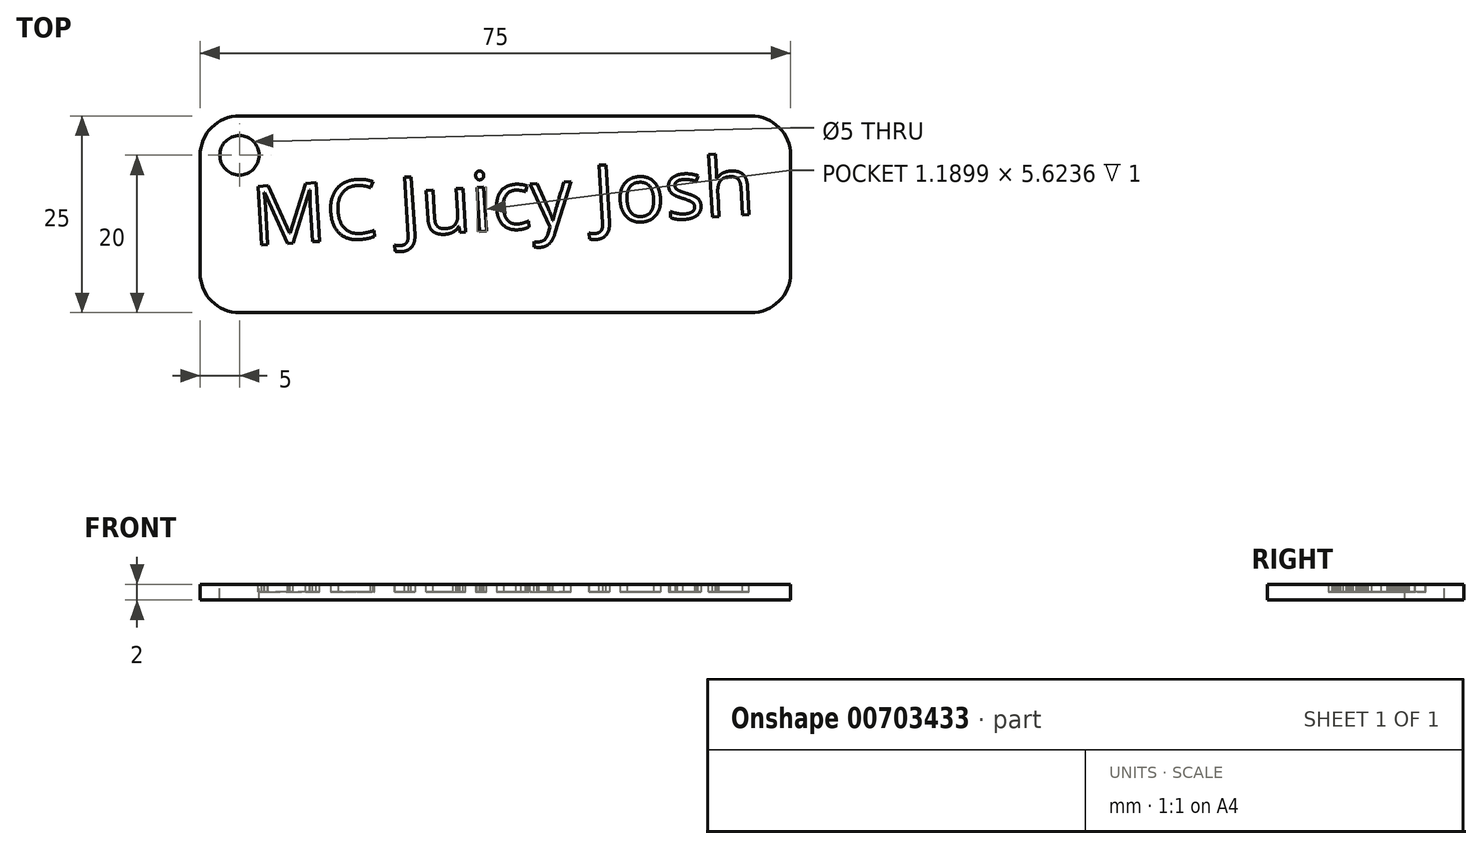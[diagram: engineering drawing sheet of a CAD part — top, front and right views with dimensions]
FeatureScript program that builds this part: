
annotation { "Feature Type Name" : "Feature", "Feature Type Description" : "" }
export const myFeature = defineFeature(function(context is Context, id is Id, definition is map)
    precondition{}
    {
        {
            var Q0;
            Q0=qCreatedBy(makeId("Top.planeOp"),FACE);
            var sketch = newSketch(context, id + "F0", { "sketchPlane" : qUnion([Q0])});
            skLineSegment(sketch, "E0.bottom", {"start": v(-32.5, 12.5) * mm, "end": v(32.5, 12.5) * mm});
            skLineSegment(sketch, "E0.top", {"start": v(-32.5, -12.5) * mm, "end": v(32.5, -12.5) * mm});
            skLineSegment(sketch, "E0.left", {"start": v(-37.5, 7.5) * mm, "end": v(-37.5, -7.5) * mm});
            skLineSegment(sketch, "E0.right", {"start": v(37.5, 7.5) * mm, "end": v(37.5, -7.5) * mm});
            skPoint(sketch, "E0.middle", {"position": v(0, 0) * mm});
            skPoint(sketch, "E1.visualSharp", {"position": v(-37.5, 12.5) * mm});
            skArc(sketch, "E1.filletArc", {"start": v(-32.5, 12.5) * mm, "mid": v(-36.04, 11.04) * mm, "end": v(-37.5, 7.5) * mm});
            skPoint(sketch, "E2.visualSharp", {"position": v(-37.5, -12.5) * mm});
            skArc(sketch, "E2.filletArc", {"start": v(-37.5, -7.5) * mm, "mid": v(-36.04, -11.04) * mm, "end": v(-32.5, -12.5) * mm});
            skPoint(sketch, "E3.visualSharp", {"position": v(37.5, -12.5) * mm});
            skArc(sketch, "E3.filletArc", {"start": v(32.5, -12.5) * mm, "mid": v(36.04, -11.04) * mm, "end": v(37.5, -7.5) * mm});
            skPoint(sketch, "E4.visualSharp", {"position": v(37.5, 12.5) * mm});
            skArc(sketch, "E4.filletArc", {"start": v(37.5, 7.5) * mm, "mid": v(36.04, 11.04) * mm, "end": v(32.5, 12.5) * mm});
            skSolve(sketch);
        }
        {
            var Q0;
            Q0=makeQuery(id+"F0.imprint","IMPRINT",FACE,{"disambiguationData":[TD([[makeQuery(id+"F0.imprint","IMPRINT",EDGE,{"derivedFrom":sQuery(id+"F0.wireOp",EDGE,"E0.bottom")}),-1.0]])]});
            extrude(context, id + "F1", {"entities" : qUnion([Q0]), "depth" : 2 * mm, "offsetDistance" : 25.4 * mm});
        }
        {
            var Q0;
            Q0=makeQuery(id+"F1.opExtrude","CAP_FACE",FACE,{"disambiguationData":[OSD([sQuery(id+"F0.wireOp",EDGE,"E0.bottom"),sQuery(id+"F0.wireOp",EDGE,"E0.top"),sQuery(id+"F0.wireOp",EDGE,"E0.left"),sQuery(id+"F0.wireOp",EDGE,"E0.right"),sQuery(id+"F0.wireOp",EDGE,"E1.filletArc"),sQuery(id+"F0.wireOp",EDGE,"E2.filletArc"),sQuery(id+"F0.wireOp",EDGE,"E3.filletArc"),sQuery(id+"F0.wireOp",EDGE,"E4.filletArc")])],"isStart":false});
            var sketch = newSketch(context, id + "F2", { "sketchPlane" : qUnion([Q0])});
            skPoint(sketch, "E5", {"position": v(-32.5, 7.5) * mm});
            skSolve(sketch);
        }
        {
            var Q0;
            Q0=sQuery(id+"F2.wireOp",VERTEX,"E5");
            var Q1;
            Q1=makeQuery(id+"F1.opExtrude","SWEPT_BODY",BODY,{"disambiguationData":[OSD([sQuery(id+"F0.wireOp",EDGE,"E0.bottom"),sQuery(id+"F0.wireOp",EDGE,"E0.top"),sQuery(id+"F0.wireOp",EDGE,"E0.left"),sQuery(id+"F0.wireOp",EDGE,"E0.right"),sQuery(id+"F0.wireOp",EDGE,"E1.filletArc"),sQuery(id+"F0.wireOp",EDGE,"E2.filletArc"),sQuery(id+"F0.wireOp",EDGE,"E3.filletArc"),sQuery(id+"F0.wireOp",EDGE,"E4.filletArc")])]});
            hole(context, id + "F3", {"style" : HoleStyle.SIMPLE, "endStyle" : HoleEndStyle.THROUGH, "holeDiameter" : 5 * mm, "majorDiameter" : 6.35 * mm, "isTappedThrough" : true, "tappedDepth" : 12.7 * mm, "tapClearance" : 3, "locations" : qUnion([Q0]), "scope" : qUnion([Q1])});
        }
        {
            var Q0;
            Q0=makeQuery(id+"F1.opExtrude","CAP_FACE",FACE,{"disambiguationData":[OSD([sQuery(id+"F0.wireOp",EDGE,"E0.bottom"),sQuery(id+"F0.wireOp",EDGE,"E0.top"),sQuery(id+"F0.wireOp",EDGE,"E0.left"),sQuery(id+"F0.wireOp",EDGE,"E0.right"),sQuery(id+"F0.wireOp",EDGE,"E1.filletArc"),sQuery(id+"F0.wireOp",EDGE,"E2.filletArc"),sQuery(id+"F0.wireOp",EDGE,"E3.filletArc"),sQuery(id+"F0.wireOp",EDGE,"E4.filletArc")])],"isStart":false});
            var sketch = newSketch(context, id + "F4", { "sketchPlane" : qUnion([Q0])});
            skText(sketch, "E6", { "text": "MC Juicy Josh", "fontName": "OpenSans-Regular.ttf"});
            const initialGuessF4  = {"E6": [-0.03072, -0.00395, 0.99808, 0.06192, 0.00751]};
            skSetInitialGuess(sketch, initialGuessF4);
            skSolve(sketch);
        }
        {
            var Q0;
            Q0 = qSketchRegion(id + "F4", true);
            extrude(context, id + "F5", {"entities" : qUnion([Q0]), "operationType" : NewBodyOperationType.REMOVE, "oppositeDirection" : true, "depth" : 1 * mm, "offsetDistance" : 25.4 * mm});
        }
    });
